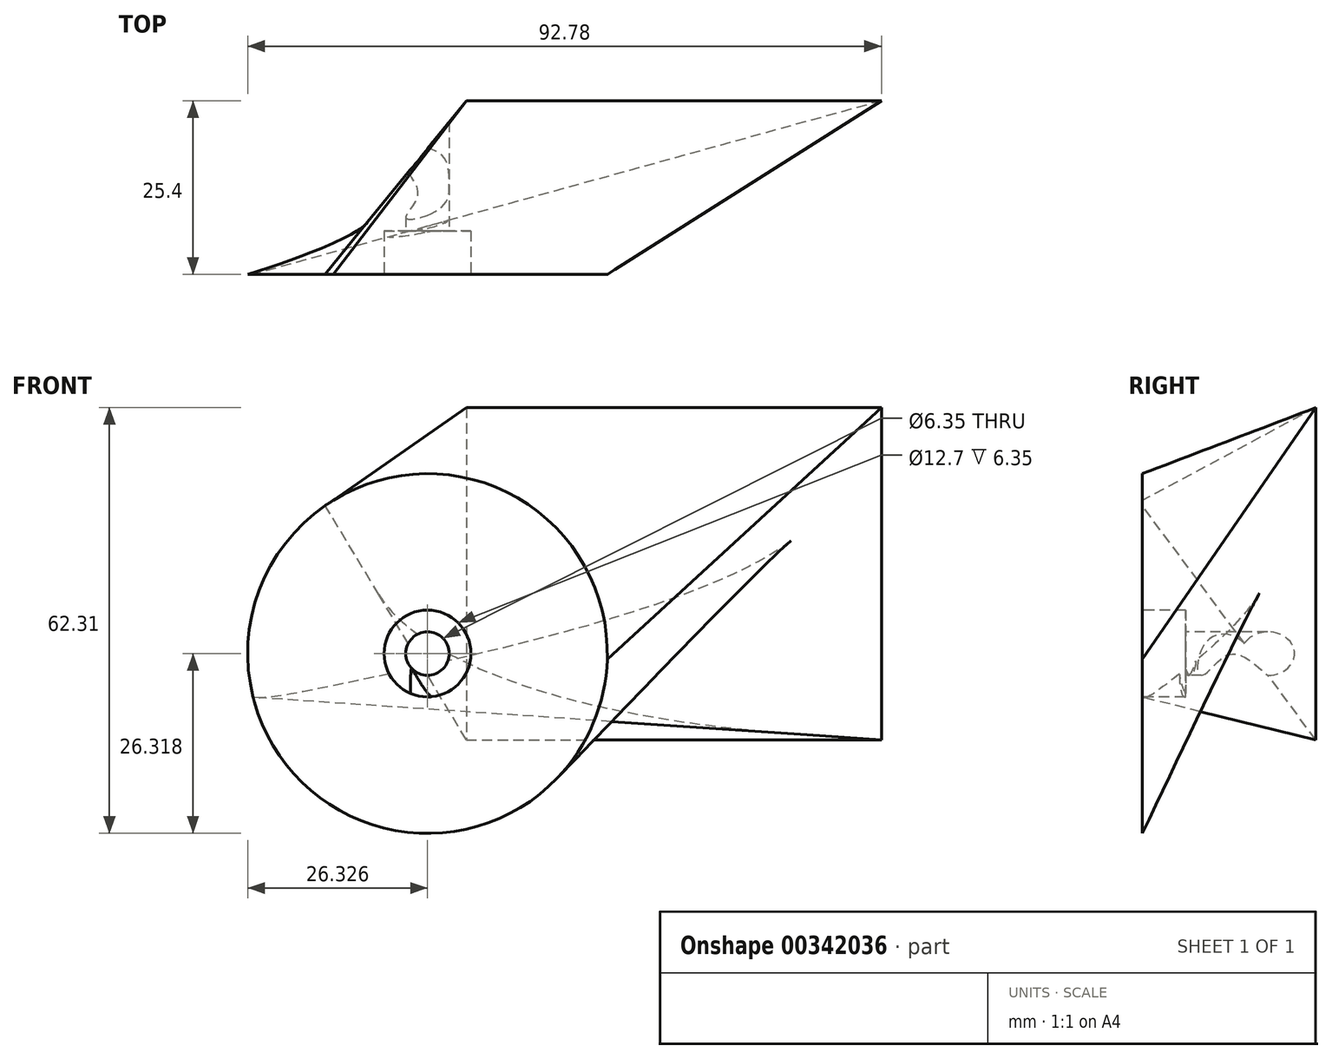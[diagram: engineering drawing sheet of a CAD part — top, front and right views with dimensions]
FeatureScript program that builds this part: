
annotation { "Feature Type Name" : "Feature", "Feature Type Description" : "" }
export const myFeature = defineFeature(function(context is Context, id is Id, definition is map)
    precondition{}
    {
        {
            var Q0;
            Q0=qCreatedBy(makeId("Front.planeOp"),FACE);
            var sketch = newSketch(context, id + "F0", { "sketchPlane" : qUnion([Q0])});
            skLineSegment(sketch, "E0.bottom", {"start": v(-30.3, 27.45) * mm, "end": v(30.48, 27.45) * mm});
            skLineSegment(sketch, "E0.top", {"start": v(-30.3, -21.16) * mm, "end": v(30.48, -21.16) * mm});
            skLineSegment(sketch, "E0.left", {"start": v(-30.3, 27.45) * mm, "end": v(-30.3, -21.16) * mm});
            skLineSegment(sketch, "E0.right", {"start": v(30.48, 27.45) * mm, "end": v(30.48, -21.16) * mm});
            skSolve(sketch);
        }
        {
            var Q0;
            Q0=qCreatedBy(makeId("Front.planeOp"),FACE);
            cPlane(context, id + "F1", {"entities" : qUnion([Q0]), "cplaneType" : CPlaneType.OFFSET, "offset" : 25.4 * mm, "width" : 152.4 * mm, "height" : 152.4 * mm});
        }
        {
            var Q0;
            Q0=qCreatedBy(id+"F1.planeOp",FACE);
            var sketch = newSketch(context, id + "F2", { "sketchPlane" : qUnion([Q0])});
            skLineSegment(sketch, "E1", {"start": v(-50.95, 13.1) * mm, "end": v(-50.95, 29.03) * mm, "construction": true});
            skLineSegment(sketch, "E2", {"start": v(-50.95, 29.03) * mm, "end": v(-9.66, -9.35) * mm, "construction": true});
            skLineSegment(sketch, "E3", {"start": v(-9.66, -9.35) * mm, "end": v(-47.1, -30.4) * mm, "construction": true});
            skLineSegment(sketch, "E4", {"start": v(-48.95, -31.44) * mm, "end": v(-61.33, -15.62) * mm, "construction": true});
            skArc(sketch, "E5", {"start": v(-49.78, 13.87) * mm, "mid": v(-50.37, 13.5) * mm, "end": v(-50.95, 13.1) * mm});
            skArc(sketch, "E6", {"start": v(-9.66, -9.35) * mm, "mid": v(-22.79, 14.24) * mm, "end": v(-49.78, 13.87) * mm});
            skLineSegment(sketch, "E7", {"start": v(-47.1, -30.4) * mm, "end": v(-48.95, -31.44) * mm, "construction": true});
            skArc(sketch, "E8", {"start": v(-61.5, -14.96) * mm, "mid": v(-61.42, -15.29) * mm, "end": v(-61.33, -15.62) * mm});
            skLineSegment(sketch, "E9", {"start": v(-48.95, -31.44) * mm, "end": v(-48.95, -31.44) * mm});
            skArc(sketch, "E10", {"start": v(-61.33, -15.62) * mm, "mid": v(-32.8, -34.67) * mm, "end": v(-9.66, -9.35) * mm});
            skArc(sketch, "E11", {"start": v(-50.95, 13.1) * mm, "mid": v(-60.61, 0.72) * mm, "end": v(-61.5, -14.96) * mm});
            skLineSegment(sketch, "E12", {"start": v(-9.66, -9.35) * mm, "end": v(-9.66, -9.35) * mm});
            skSolve(sketch);
        }
        {
            var Q0;
            Q0=makeQuery(id+"F0.imprint","IMPRINT",FACE,{"disambiguationData":[TD([[makeQuery(id+"F0.imprint","IMPRINT",EDGE,{"derivedFrom":sQuery(id+"F0.wireOp",EDGE,"E0.bottom")}),-1.0]])]});
            var Q1;
            Q1=makeQuery(id+"F2.imprint","IMPRINT",FACE,{"disambiguationData":[TD([[makeQuery(id+"F2.imprint","IMPRINT",EDGE,{"derivedFrom":sQuery(id+"F2.wireOp",EDGE,"E5")}),1.0]])]});
            loft(context, id + "F3", {"sheetProfilesArray" : [{ "sheetProfileEntities" : qUnion([Q0]) }, { "sheetProfileEntities" : qUnion([Q1]) }]});
        }
        {
            var Q0;
            Q0=makeQuery(id+"F3.opLoft","CAP_FACE",FACE,{"disambiguationData":[OSD([makeQuery(id+"F2.imprint","IMPRINT",FACE,{"disambiguationData":[TD([[makeQuery(id+"F2.imprint","IMPRINT",EDGE,{"derivedFrom":sQuery(id+"F2.wireOp",EDGE,"E5")}),1.0]])]})])],"isStart":true});
            var sketch = newSketch(context, id + "F4", { "sketchPlane" : qUnion([Q0])});
            skPoint(sketch, "E13", {"position": v(-35.97, -8.54) * mm});
            skSolve(sketch);
        }
        {
            var Q0;
            Q0=sQuery(id+"F4.wireOp",VERTEX,"E13");
            var Q1;
            Q1=makeQuery(id+"F3.opLoft","SWEPT_BODY",BODY,{"disambiguationData":[OSD([makeQuery(id+"F0.imprint","IMPRINT",FACE,{"disambiguationData":[TD([[makeQuery(id+"F0.imprint","IMPRINT",EDGE,{"derivedFrom":sQuery(id+"F0.wireOp",EDGE,"E0.bottom")}),-1.0]])]}),makeQuery(id+"F2.imprint","IMPRINT",FACE,{"disambiguationData":[TD([[makeQuery(id+"F2.imprint","IMPRINT",EDGE,{"derivedFrom":sQuery(id+"F2.wireOp",EDGE,"E5")}),1.0]])]})])]});
            hole(context, id + "F5", {"style" : HoleStyle.C_BORE, "endStyle" : HoleEndStyle.THROUGH, "holeDiameter" : 6.35 * mm, "cBoreDiameter" : 12.7 * mm, "cBoreDepth" : 6.35 * mm, "isTappedThrough" : true, "tappedDepth" : 12.7 * mm, "tapClearance" : 3, "locations" : qUnion([Q0]), "scope" : qUnion([Q1])});
        }
    });
